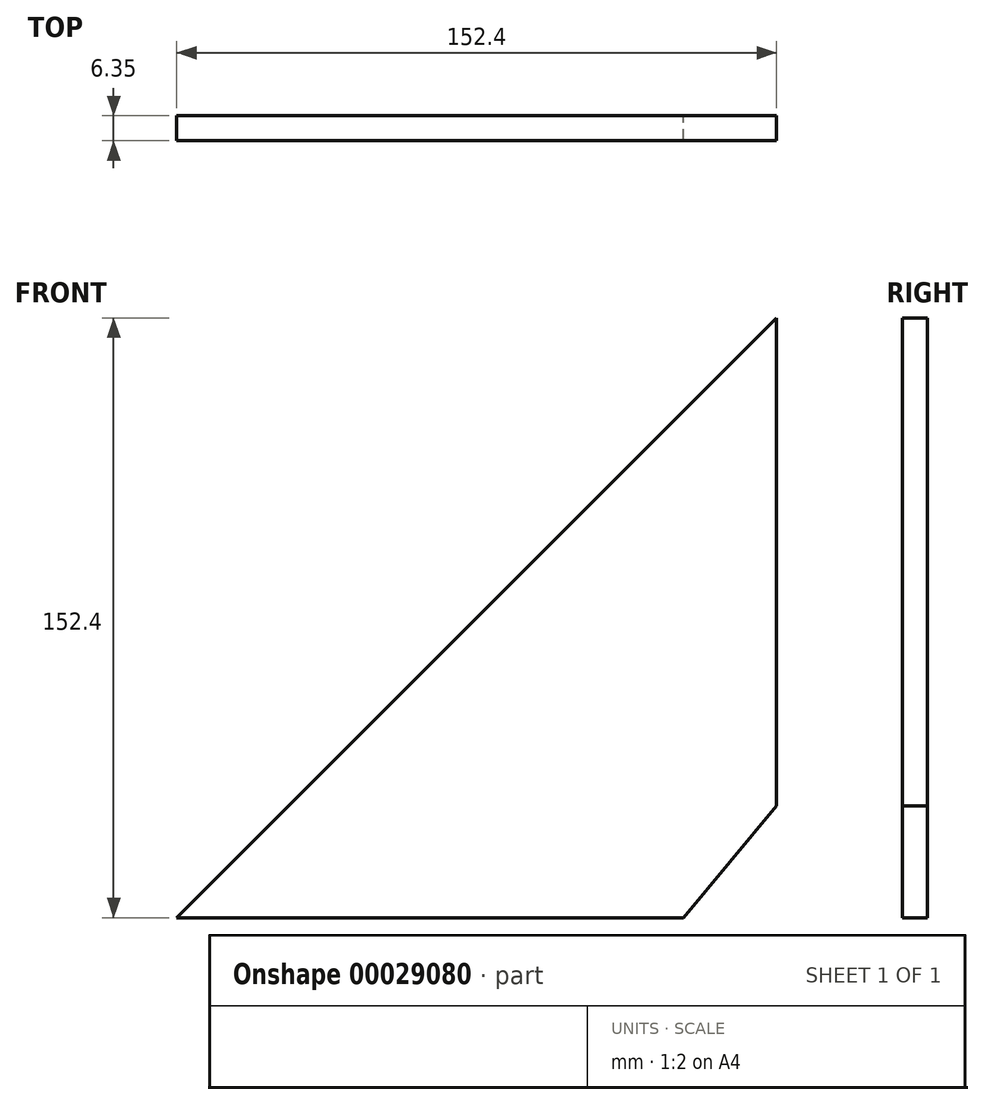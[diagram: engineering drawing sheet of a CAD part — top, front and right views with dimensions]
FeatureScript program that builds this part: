
annotation { "Feature Type Name" : "Feature", "Feature Type Description" : "" }
export const myFeature = defineFeature(function(context is Context, id is Id, definition is map)
    precondition{}
    {
        {
            var Q0;
            Q0=qCreatedBy(makeId("Front.planeOp"),FACE);
            var sketch = newSketch(context, id + "F0", { "sketchPlane" : qUnion([Q0])});
            skLineSegment(sketch, "E0", {"start": v(0, 0) * mm, "end": v(128.77, 0) * mm});
            skLineSegment(sketch, "E1", {"start": v(152.4, 28.44) * mm, "end": v(152.4, 152.4) * mm});
            skLineSegment(sketch, "E2", {"start": v(152.4, 28.44) * mm, "end": v(128.77, 0) * mm});
            skPoint(sketch, "E3.orphan", {"position": v(152.4, 0) * mm});
            skLineSegment(sketch, "E4", {"start": v(152.4, 152.4) * mm, "end": v(0, 0) * mm});
            skSolve(sketch);
        }
        {
            var Q0;
            Q0=makeQuery(id+"F0.imprint","IMPRINT",FACE,{"disambiguationData":[TD([[makeQuery(id+"F0.imprint","IMPRINT",EDGE,{"derivedFrom":sQuery(id+"F0.wireOp",EDGE,"E0")}),1.0]])]});
            extrude(context, id + "F1", {"entities" : qUnion([Q0]), "depth" : 6.35 * mm});
        }
    });
